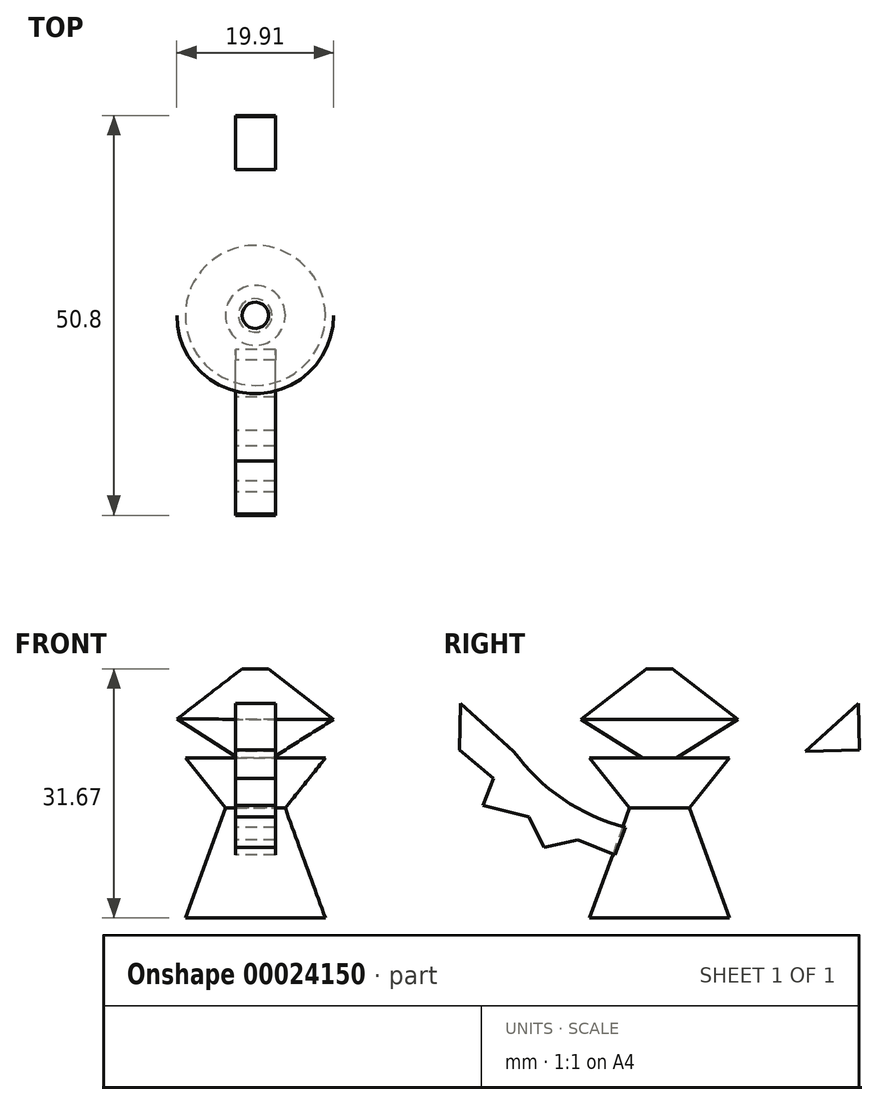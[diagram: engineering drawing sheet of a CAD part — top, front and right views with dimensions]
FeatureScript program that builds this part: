
annotation { "Feature Type Name" : "Feature", "Feature Type Description" : "" }
export const myFeature = defineFeature(function(context is Context, id is Id, definition is map)
    precondition{}
    {
        {
            var Q0;
            Q0=qCreatedBy(makeId("Top.planeOp"),FACE);
            var sketch = newSketch(context, id + "F0", { "sketchPlane" : qUnion([Q0])});
            skCircle(sketch, "E0", {"center": v(0, 0) * mm, "radius": 8.9 * mm});
            skSolve(sketch);
        }
        {
            var Q0;
            Q0=qCreatedBy(makeId("Top.planeOp"),FACE);
            cPlane(context, id + "F1", {"entities" : qUnion([Q0]), "cplaneType" : CPlaneType.OFFSET, "offset" : 13.97 * mm, "width" : 152.4 * mm, "height" : 152.4 * mm});
        }
        {
            var Q0;
            Q0=qCreatedBy(id+"F1.planeOp",FACE);
            var sketch = newSketch(context, id + "F2", { "sketchPlane" : qUnion([Q0])});
            skCircle(sketch, "E1", {"center": v(0, 0) * mm, "radius": 3.81 * mm});
            skSolve(sketch);
        }
        {
            var Q0;
            Q0=makeQuery(id+"F0.imprint","IMPRINT",FACE,{"disambiguationData":[TD([[makeQuery(id+"F0.imprint","IMPRINT",EDGE,{"derivedFrom":sQuery(id+"F0.wireOp",EDGE,"E0")}),1.0]])]});
            var Q1;
            Q1=makeQuery(id+"F2.imprint","IMPRINT",FACE,{"disambiguationData":[TD([[makeQuery(id+"F2.imprint","IMPRINT",EDGE,{"derivedFrom":sQuery(id+"F2.wireOp",EDGE,"E1")}),1.0]])]});
            loft(context, id + "F3", {"sheetProfilesArray" : [{ "sheetProfileEntities" : qUnion([Q0]) }, { "sheetProfileEntities" : qUnion([Q1]) }]});
        }
        {
            var Q0;
            Q0=qCreatedBy(id+"F1.planeOp",FACE);
            cPlane(context, id + "F4", {"entities" : qUnion([Q0]), "cplaneType" : CPlaneType.OFFSET, "offset" : 6.35 * mm, "width" : 152.4 * mm, "height" : 152.4 * mm});
        }
        {
            var Q0;
            Q0=qCreatedBy(id+"F4.planeOp",FACE);
            var sketch = newSketch(context, id + "F5", { "sketchPlane" : qUnion([Q0])});
            skCircle(sketch, "E2", {"center": v(0, 0) * mm, "radius": 8.9 * mm});
            skSolve(sketch);
        }
        {
            var Q1;
            Q1=makeQuery(id+"F3.opLoft","CAP_FACE",FACE,{"disambiguationData":[OSD([makeQuery(id+"F2.imprint","IMPRINT",FACE,{"disambiguationData":[TD([[makeQuery(id+"F2.imprint","IMPRINT",EDGE,{"derivedFrom":sQuery(id+"F2.wireOp",EDGE,"E1")}),1.0]])]})])],"isStart":true});
            var Q2;
            Q2=makeQuery(id+"F5.imprint","IMPRINT",FACE,{"disambiguationData":[TD([[makeQuery(id+"F5.imprint","IMPRINT",EDGE,{"derivedFrom":sQuery(id+"F5.wireOp",EDGE,"E2")}),1.0]])]});
            loft(context, id + "F6", {"operationType" : NewBodyOperationType.ADD, "sheetProfilesArray" : [{ "sheetProfileEntities" : qUnion([Q1]) }, { "sheetProfileEntities" : qUnion([Q2]) }]});
        }
        {
            var Q0;
            Q0=qCreatedBy(makeId("Front.planeOp"),FACE);
            var sketch = newSketch(context, id + "F7", { "sketchPlane" : qUnion([Q0])});
            skLineSegment(sketch, "E3", {"start": v(-8.9, 18.97) * mm, "end": v(8.85, 18.97) * mm});
            skLineSegment(sketch, "E4", {"start": v(-0.02, 18.97) * mm, "end": v(0, 31.67) * mm});
            skLineSegment(sketch, "E5.MirrorCS", {"start": v(-0.02, 18.97) * mm, "end": v(9.94, 25.24) * mm});
            skLineSegment(sketch, "E6.MirrorCS", {"start": v(9.94, 25.24) * mm, "end": v(3.62, 30.15) * mm});
            skLineSegment(sketch, "E7", {"start": v(0, 31.67) * mm, "end": v(1.67, 31.66) * mm});
            skLineSegment(sketch, "E8", {"start": v(3.62, 30.15) * mm, "end": v(1.67, 31.66) * mm});
            skPoint(sketch, "E9.MirrorCS.end.orphan", {"position": v(-1.67, 31.67) * mm});
            skPoint(sketch, "E9.MirrorCS.start.orphan", {"position": v(-3.63, 30.16) * mm});
            skPoint(sketch, "E10.end.orphan", {"position": v(-9.97, 25.28) * mm});
            skSolve(sketch);
        }
        {
            var Q0;
            Q0=makeQuery(id+"F7.imprint","IMPRINT",FACE,{"disambiguationData":[TD([[makeQuery(id+"F7.imprint","IMPRINT",EDGE,{"derivedFrom":sQuery(id+"F7.wireOp",EDGE,"E4")}),-1.0]])]});
            var Q1;
            Q1=sQuery(id+"F7.wireOp",EDGE,"E4");
            revolve(context, id + "F8", {"operationType" : NewBodyOperationType.ADD, "entities" : qUnion([Q0]), "axis" : qUnion([Q1]), "revolveType" : RevolveType.FULL});
        }
        {
            var Q0;
            Q0=qCreatedBy(makeId("Right.planeOp"),FACE);
            var sketch = newSketch(context, id + "F9", { "sketchPlane" : qUnion([Q0])});
            skArc(sketch, "E11", {"start": v(-18.51, 21.2) * mm, "mid": v(-12.27, 15.12) * mm, "end": v(-4.31, 11.54) * mm});
            skArc(sketch, "E12.MirrorCS", {"start": v(18.51, 21.2) * mm, "mid": v(12.27, 15.12) * mm, "end": v(4.31, 11.54) * mm});
            skLineSegment(sketch, "E13", {"start": v(-18.51, 21.2) * mm, "end": v(-25.4, 21.34) * mm});
            skLineSegment(sketch, "E14.MirrorCS", {"start": v(18.51, 21.2) * mm, "end": v(25.4, 21.34) * mm});
            skLineSegment(sketch, "E15", {"start": v(-25.4, 21.34) * mm, "end": v(-21.07, 17.78) * mm});
            skLineSegment(sketch, "E16", {"start": v(-21.07, 17.78) * mm, "end": v(-22.45, 14.32) * mm});
            skLineSegment(sketch, "E17", {"start": v(-22.45, 14.32) * mm, "end": v(-16.57, 12.83) * mm});
            skLineSegment(sketch, "E18", {"start": v(-16.57, 12.83) * mm, "end": v(-14.65, 9) * mm});
            skLineSegment(sketch, "E19", {"start": v(-14.65, 9) * mm, "end": v(-10.36, 9.95) * mm});
            skLineSegment(sketch, "E20", {"start": v(-10.36, 9.95) * mm, "end": v(-5.65, 8) * mm});
            skLineSegment(sketch, "E21.MirrorCS", {"start": v(25.4, 21.34) * mm, "end": v(21.07, 17.78) * mm});
            skLineSegment(sketch, "E22.MirrorCS", {"start": v(21.07, 17.78) * mm, "end": v(22.45, 14.32) * mm});
            skLineSegment(sketch, "E23.MirrorCS", {"start": v(22.45, 14.32) * mm, "end": v(16.57, 12.83) * mm});
            skLineSegment(sketch, "E24.MirrorCS", {"start": v(16.57, 12.83) * mm, "end": v(14.65, 9) * mm});
            skLineSegment(sketch, "E25.MirrorCS", {"start": v(14.65, 9) * mm, "end": v(10.36, 9.95) * mm});
            skLineSegment(sketch, "E26.MirrorCS", {"start": v(10.36, 9.95) * mm, "end": v(5.65, 8) * mm});
            skLineSegment(sketch, "E27", {"start": v(-4.31, 11.54) * mm, "end": v(-5.65, 8) * mm});
            skLineSegment(sketch, "E28", {"start": v(4.31, 11.54) * mm, "end": v(5.65, 8) * mm});
            skLineSegment(sketch, "E29", {"start": v(-18.51, 21.2) * mm, "end": v(-25.26, 27.3) * mm});
            skLineSegment(sketch, "E30", {"start": v(-25.26, 27.3) * mm, "end": v(-25.4, 21.34) * mm});
            skLineSegment(sketch, "E31.MirrorCS", {"start": v(18.51, 21.2) * mm, "end": v(25.26, 27.3) * mm});
            skLineSegment(sketch, "E32.MirrorCS", {"start": v(25.26, 27.3) * mm, "end": v(25.4, 21.34) * mm});
            skSolve(sketch);
        }
        {
            var Q0;
            Q0=makeQuery(id+"F9.imprint","IMPRINT",FACE,{"disambiguationData":[TD([[makeQuery(id+"F9.imprint","IMPRINT",EDGE,{"derivedFrom":sQuery(id+"F9.wireOp",EDGE,"E11")}),-1.0]])]});
            var Q1;
            Q1=makeQuery(id+"F9.imprint","IMPRINT",FACE,{"disambiguationData":[TD([[makeQuery(id+"F9.imprint","IMPRINT",EDGE,{"derivedFrom":sQuery(id+"F9.wireOp",EDGE,"E12.MirrorCS")}),1.0]])]});
            var Q2;
            Q2=makeQuery(id+"F9.imprint","IMPRINT",FACE,{"disambiguationData":[TD([[makeQuery(id+"F9.imprint","IMPRINT",EDGE,{"derivedFrom":sQuery(id+"F9.wireOp",EDGE,"E13")}),-1.0]])]});
            var Q3;
            Q3=makeQuery(id+"F9.imprint","IMPRINT",FACE,{"disambiguationData":[TD([[makeQuery(id+"F9.imprint","IMPRINT",EDGE,{"derivedFrom":sQuery(id+"F9.wireOp",EDGE,"E14.MirrorCS")}),1.0]])]});
            extrude(context, id + "F10", {"entities" : qUnion([Q0, Q1, Q2, Q3]), "endBound" : BoundingType.SYMMETRIC, "depth" : 5.08 * mm});
        }
    });
